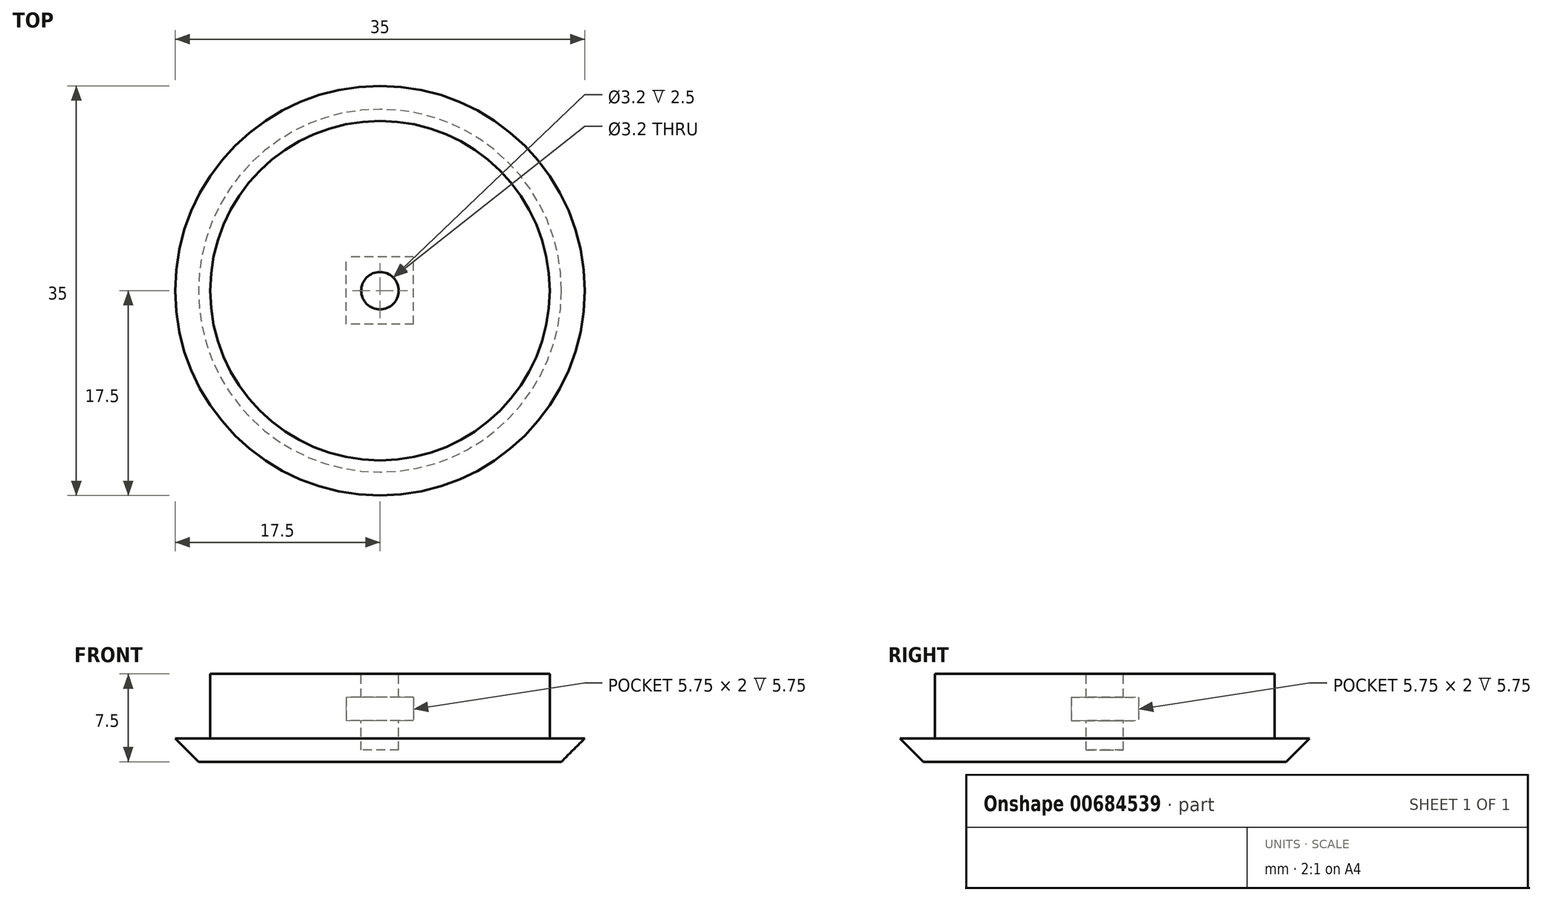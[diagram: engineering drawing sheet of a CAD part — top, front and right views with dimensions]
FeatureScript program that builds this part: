
annotation { "Feature Type Name" : "Feature", "Feature Type Description" : "" }
export const myFeature = defineFeature(function(context is Context, id is Id, definition is map)
    precondition{}
    {
        {
            var Q0;
            Q0=qCreatedBy(makeId("Top.planeOp"),FACE);
            var sketch = newSketch(context, id + "F0", { "sketchPlane" : qUnion([Q0])});
            skCircle(sketch, "E0", {"center": v(0, 0) * mm, "radius": 17.5 * mm});
            skSolve(sketch);
        }
        {
            var Q0;
            Q0=makeQuery(id+"F0.imprint","IMPRINT",FACE,{"disambiguationData":[TD([[makeQuery(id+"F0.imprint","IMPRINT",EDGE,{"derivedFrom":sQuery(id+"F0.wireOp",EDGE,"E0")}),1.0]])]});
            extrude(context, id + "F1", {"entities" : qUnion([Q0]), "depth" : 2 * mm, "offsetDistance" : 25 * mm});
        }
        {
            var Q0;
            Q0=makeQuery(id+"F1.opExtrude","CAP_FACE",FACE,{"disambiguationData":[OSD([sQuery(id+"F0.wireOp",EDGE,"E0")])],"isStart":false});
            var sketch = newSketch(context, id + "F2", { "sketchPlane" : qUnion([Q0])});
            skCircle(sketch, "E1", {"center": v(0, 0) * mm, "radius": 14.5 * mm});
            skSolve(sketch);
        }
        {
            var Q0;
            Q0=makeQuery(id+"F2.imprint","IMPRINT",FACE,{"disambiguationData":[TD([[makeQuery(id+"F2.imprint","IMPRINT",EDGE,{"derivedFrom":sQuery(id+"F2.wireOp",EDGE,"E1")}),1.0]])]});
            extrude(context, id + "F3", {"entities" : qUnion([Q0]), "operationType" : NewBodyOperationType.ADD, "depth" : 5.5 * mm, "offsetDistance" : 25 * mm});
        }
        {
            var Q0;
            Q0=makeQuery(id+"F3.opExtrude","CAP_FACE",FACE,{"disambiguationData":[OSD([sQuery(id+"F2.wireOp",EDGE,"E1")])],"isStart":false});
            var sketch = newSketch(context, id + "F4", { "sketchPlane" : qUnion([Q0])});
            skLineSegment(sketch, "E2.bottom", {"start": v(2.88, -2.87) * mm, "end": v(-2.87, -2.88) * mm});
            skLineSegment(sketch, "E2.top", {"start": v(2.87, 2.88) * mm, "end": v(-2.88, 2.87) * mm});
            skLineSegment(sketch, "E2.left", {"start": v(2.88, -2.87) * mm, "end": v(2.87, 2.88) * mm});
            skLineSegment(sketch, "E2.right", {"start": v(-2.87, -2.88) * mm, "end": v(-2.88, 2.87) * mm});
            skPoint(sketch, "E2.middle", {"position": v(0, 0) * mm});
            skLineSegment(sketch, "E3.bottom", {"start": v(-2.88, 2.87) * mm, "end": v(2.88, 2.87) * mm});
            skLineSegment(sketch, "E3.top", {"start": v(-2.88, 15.66) * mm, "end": v(2.88, 15.66) * mm});
            skLineSegment(sketch, "E3.left", {"start": v(-2.88, 2.87) * mm, "end": v(-2.88, 15.66) * mm});
            skLineSegment(sketch, "E3.right", {"start": v(2.88, 2.87) * mm, "end": v(2.88, 15.66) * mm});
            skSolve(sketch);
        }
        {
            var Q0;
            {var subQ0=sQuery(id+"F4.wireOp",EDGE,"E3.bottom");Q0=makeQuery(id+"F4.imprint","IMPRINT",FACE,{"disambiguationData":[TD([[makeQuery(id+"F4.imprint","IMPRINT",EDGE,{"derivedFrom":subQ0}),1.0]])]});}
            var Q1;
            Q1=makeQuery(id+"F4.imprint","IMPRINT",FACE,{"disambiguationData":[TD([[makeQuery(id+"F4.imprint","IMPRINT",EDGE,{"derivedFrom":sQuery(id+"F4.wireOp",EDGE,"E2.bottom")}),-1.0]])]});
            extrude(context, id + "F5", {"entities" : qUnion([Q0, Q1]), "depth" : 2 * mm, "offsetDistance" : 25 * mm});
        }
        {
            var Q0;
            Q0=makeQuery(id+"F5.opExtrude","SWEPT_BODY",BODY,{"disambiguationData":[OSD([sQuery(id+"F2.wireOp",EDGE,"E1"),sQuery(id+"F4.wireOp",EDGE,"E2.bottom"),sQuery(id+"F4.wireOp",EDGE,"E2.left"),sQuery(id+"F4.wireOp",EDGE,"E2.right"),sQuery(id+"F4.wireOp",EDGE,"E3.left"),sQuery(id+"F4.wireOp",EDGE,"E3.right")])]});
            transform(context, id + "F6", {"entities" : qUnion([Q0]), "transformType" : TransformType.TRANSLATION_3D, "dx" : 0 * mm, "dy" : 0 * mm, "dz" : -4 * mm, "makeCopy" : false});
        }
        {
            var Q0;
            Q0=makeQuery(id+"F5.opExtrude","SWEPT_BODY",BODY,{"disambiguationData":[OSD([sQuery(id+"F2.wireOp",EDGE,"E1"),sQuery(id+"F4.wireOp",EDGE,"E2.bottom"),sQuery(id+"F4.wireOp",EDGE,"E2.left"),sQuery(id+"F4.wireOp",EDGE,"E2.right"),sQuery(id+"F4.wireOp",EDGE,"E3.left"),sQuery(id+"F4.wireOp",EDGE,"E3.right")])]});
            var Q1;
            Q1=makeQuery(id+"F1.opExtrude","SWEPT_BODY",BODY,{"disambiguationData":[OSD([sQuery(id+"F0.wireOp",EDGE,"E0")])]});
            booleanBodies(context, id + "F7", {"operationType" : BooleanOperationType.SUBTRACTION, "tools" : qUnion([Q0]), "targets" : qUnion([Q1])});
        }
        {
            var Q0;
            Q0=makeQuery(id+"F3.opExtrude","CAP_FACE",FACE,{"disambiguationData":[OSD([sQuery(id+"F2.wireOp",EDGE,"E1")])],"isStart":false});
            var sketch = newSketch(context, id + "F8", { "sketchPlane" : qUnion([Q0])});
            skCircle(sketch, "E4", {"center": v(0, 0) * mm, "radius": 1.6 * mm});
            skSolve(sketch);
        }
        {
            var Q0;
            Q0=makeQuery(id+"F8.imprint","IMPRINT",FACE,{"disambiguationData":[TD([[makeQuery(id+"F8.imprint","IMPRINT",EDGE,{"derivedFrom":sQuery(id+"F8.wireOp",EDGE,"E4")}),1.0]])]});
            extrude(context, id + "F9", {"entities" : qUnion([Q0]), "operationType" : NewBodyOperationType.REMOVE, "oppositeDirection" : true, "depth" : 6.5 * mm, "offsetDistance" : 25 * mm});
        }
        {
            var Q0;
            Q0=makeQuery(id+"F1.opExtrude","CAP_EDGE",EDGE,{"disambiguationData":[OSD([sQuery(id+"F0.wireOp",EDGE,"E0")])],"isStart":true});
            chamfer(context, id + "F10", {"entities" : qUnion([Q0]), "width" : 2 * mm, "tangentPropagation" : true});
        }
    });
